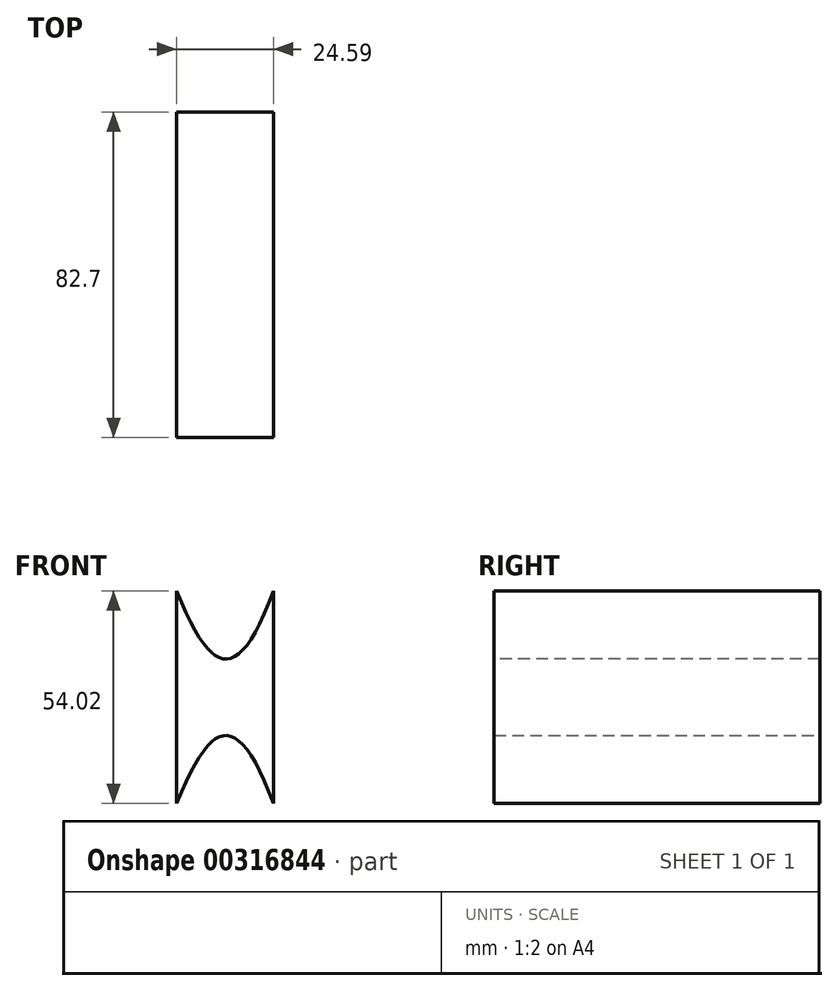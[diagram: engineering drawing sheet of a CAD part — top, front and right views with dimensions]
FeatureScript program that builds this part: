
annotation { "Feature Type Name" : "Feature", "Feature Type Description" : "" }
export const myFeature = defineFeature(function(context is Context, id is Id, definition is map)
    precondition{}
    {
        {
            var Q0;
            Q0=qCreatedBy(makeId("Front.planeOp"),FACE);
            var sketch = newSketch(context, id + "F0", { "sketchPlane" : qUnion([Q0])});
            skLineSegment(sketch, "E0.bottom", {"start": v(-9.58, 36.73) * mm, "end": v(15, 36.73) * mm});
            skLineSegment(sketch, "E0.top", {"start": v(-9.58, -17.3) * mm, "end": v(15, -17.3) * mm});
            skLineSegment(sketch, "E0.left", {"start": v(-9.58, 36.73) * mm, "end": v(-9.58, -17.3) * mm});
            skLineSegment(sketch, "E0.right", {"start": v(15, 36.73) * mm, "end": v(15, -17.3) * mm});
            skPoint(sketch, "E1.1.internal.snap0", {"position": v(2.72, 36.73) * mm});
            skFitSpline(sketch, "E1", {"points": [v(-9.58, 36.73) * mm, v(2.72, 19.44) * mm, v(15, 36.73) * mm], "startDerivative": vector(29.16, -70.32) * mm, "endDerivative": vector(27.44, 75.46) * mm});
            skLineSegment(sketch, "E2", {"start": v(-9.58, 9.72) * mm, "end": v(15, 9.72) * mm, "construction": true});
            skFitSpline(sketch, "E3.MirrorCS", {"points": [v(-9.58, -17.3) * mm, v(2.72, 0) * mm, v(15, -17.3) * mm], "startDerivative": vector(29.16, 70.32) * mm, "endDerivative": vector(27.44, -75.46) * mm});
            skLineSegment(sketch, "E4.MirrorCS", {"start": v(-9.58, -17.3) * mm, "end": v(-9.58, 36.73) * mm});
            skLineSegment(sketch, "E5.MirrorCS", {"start": v(15, -17.3) * mm, "end": v(15, 36.73) * mm});
            skSolve(sketch);
        }
        {
            var Q0;
            Q0=makeQuery(id+"F0.imprint","IMPRINT",FACE,{"disambiguationData":[TD([[makeQuery(id+"F0.imprint","IMPRINT",EDGE,{"derivedFrom":sQuery(id+"F0.wireOp",EDGE,"E1")}),-1.0]])]});
            extrude(context, id + "F1", {"entities" : qUnion([Q0]), "depth" : 82.7 * mm});
        }
    });
